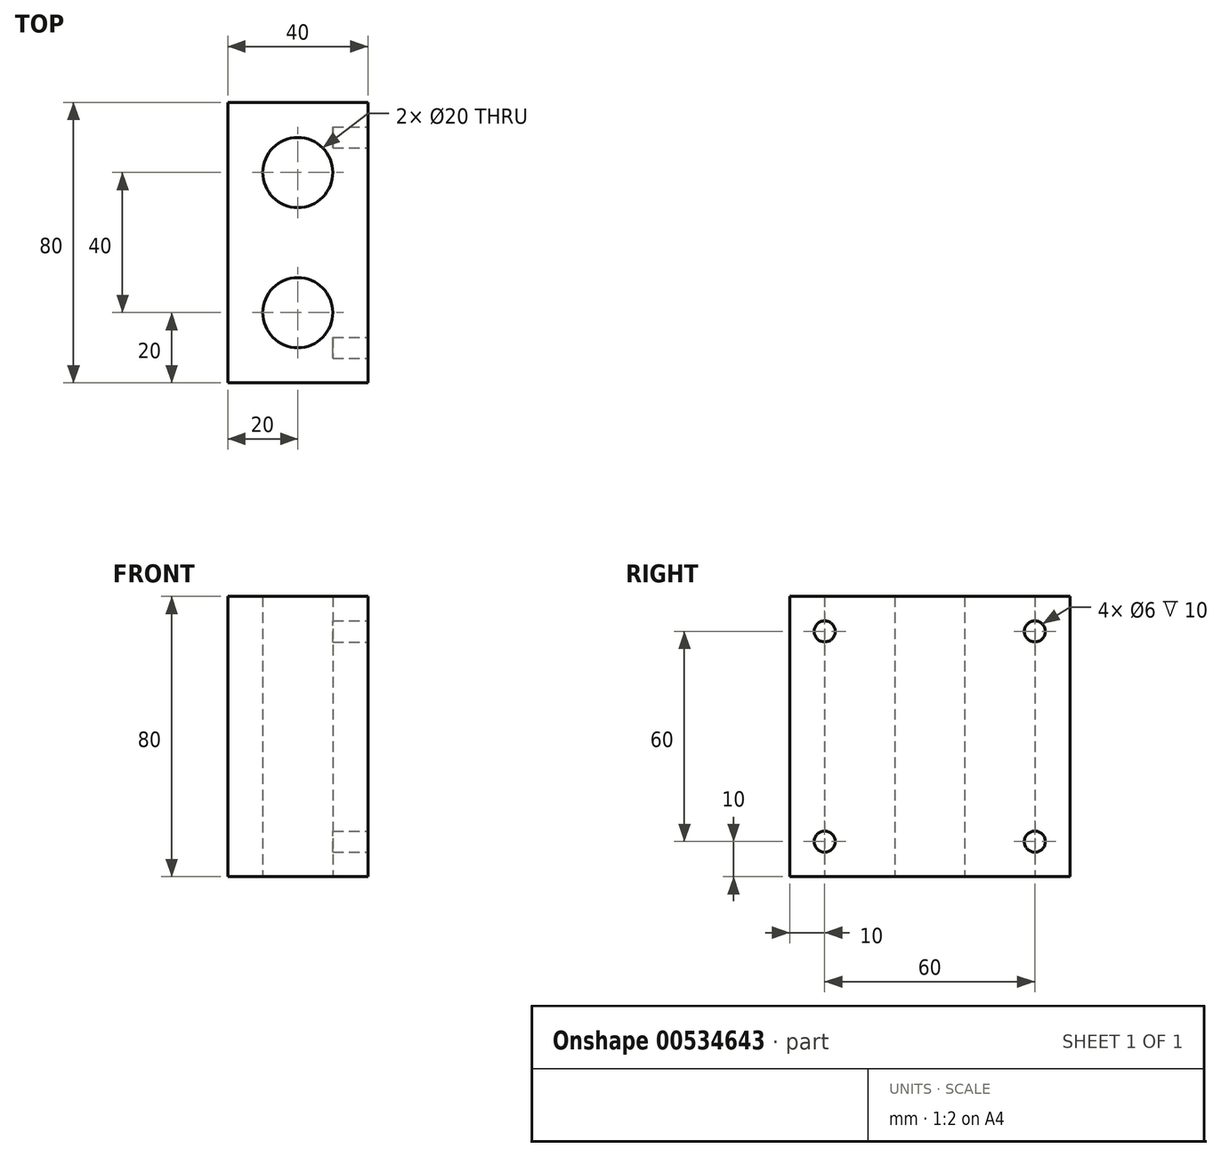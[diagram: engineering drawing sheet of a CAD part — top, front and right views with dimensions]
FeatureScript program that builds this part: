
annotation { "Feature Type Name" : "Feature", "Feature Type Description" : "" }
export const myFeature = defineFeature(function(context is Context, id is Id, definition is map)
    precondition{}
    {
        {
            var Q0;
            Q0=qCreatedBy(makeId("Top.planeOp"),FACE);
            var sketch = newSketch(context, id + "F0", { "sketchPlane" : qUnion([Q0])});
            skCircle(sketch, "E0", {"center": v(0, 20) * mm, "radius": 10 * mm});
            skCircle(sketch, "E1", {"center": v(0, -20) * mm, "radius": 10 * mm});
            skLineSegment(sketch, "E2.bottom", {"start": v(-20, 40) * mm, "end": v(20, 40) * mm});
            skLineSegment(sketch, "E2.top", {"start": v(-20, -40) * mm, "end": v(20, -40) * mm});
            skLineSegment(sketch, "E2.left", {"start": v(-20, 40) * mm, "end": v(-20, -40) * mm});
            skLineSegment(sketch, "E2.right", {"start": v(20, 40) * mm, "end": v(20, -40) * mm});
            skSolve(sketch);
        }
        {
            var Q0;
            Q0 = qSketchRegion(id + "F0", true);
            extrude(context, id + "F1", {"entities" : qUnion([Q0]), "depth" : 80 * mm, "offsetDistance" : 25 * mm});
        }
        {
            var Q0;
            Q0=makeQuery(id+"F1.opExtrude","SWEPT_FACE",FACE,{"disambiguationData":[OSD([sQuery(id+"F0.wireOp",EDGE,"E2.right")])]});
            var sketch = newSketch(context, id + "F2", { "sketchPlane" : qUnion([Q0])});
            skLineSegment(sketch, "E3", {"start": v(40, 40) * mm, "end": v(-40, 40) * mm, "construction": true});
            skLineSegment(sketch, "E4", {"start": v(0, 80) * mm, "end": v(0, 0) * mm, "construction": true});
            skCircle(sketch, "E5", {"center": v(30, 70) * mm, "radius": 3 * mm});
            skCircle(sketch, "E6", {"center": v(-30, 70) * mm, "radius": 3 * mm});
            skCircle(sketch, "E7", {"center": v(-30, 10) * mm, "radius": 3 * mm});
            skCircle(sketch, "E8", {"center": v(30, 10) * mm, "radius": 3 * mm});
            skSolve(sketch);
        }
        {
            var Q0;
            Q0 = qSketchRegion(id + "F2", true);
            extrude(context, id + "F3", {"entities" : qUnion([Q0]), "operationType" : NewBodyOperationType.REMOVE, "oppositeDirection" : true, "depth" : 10 * mm, "offsetDistance" : 25 * mm});
        }
    });
